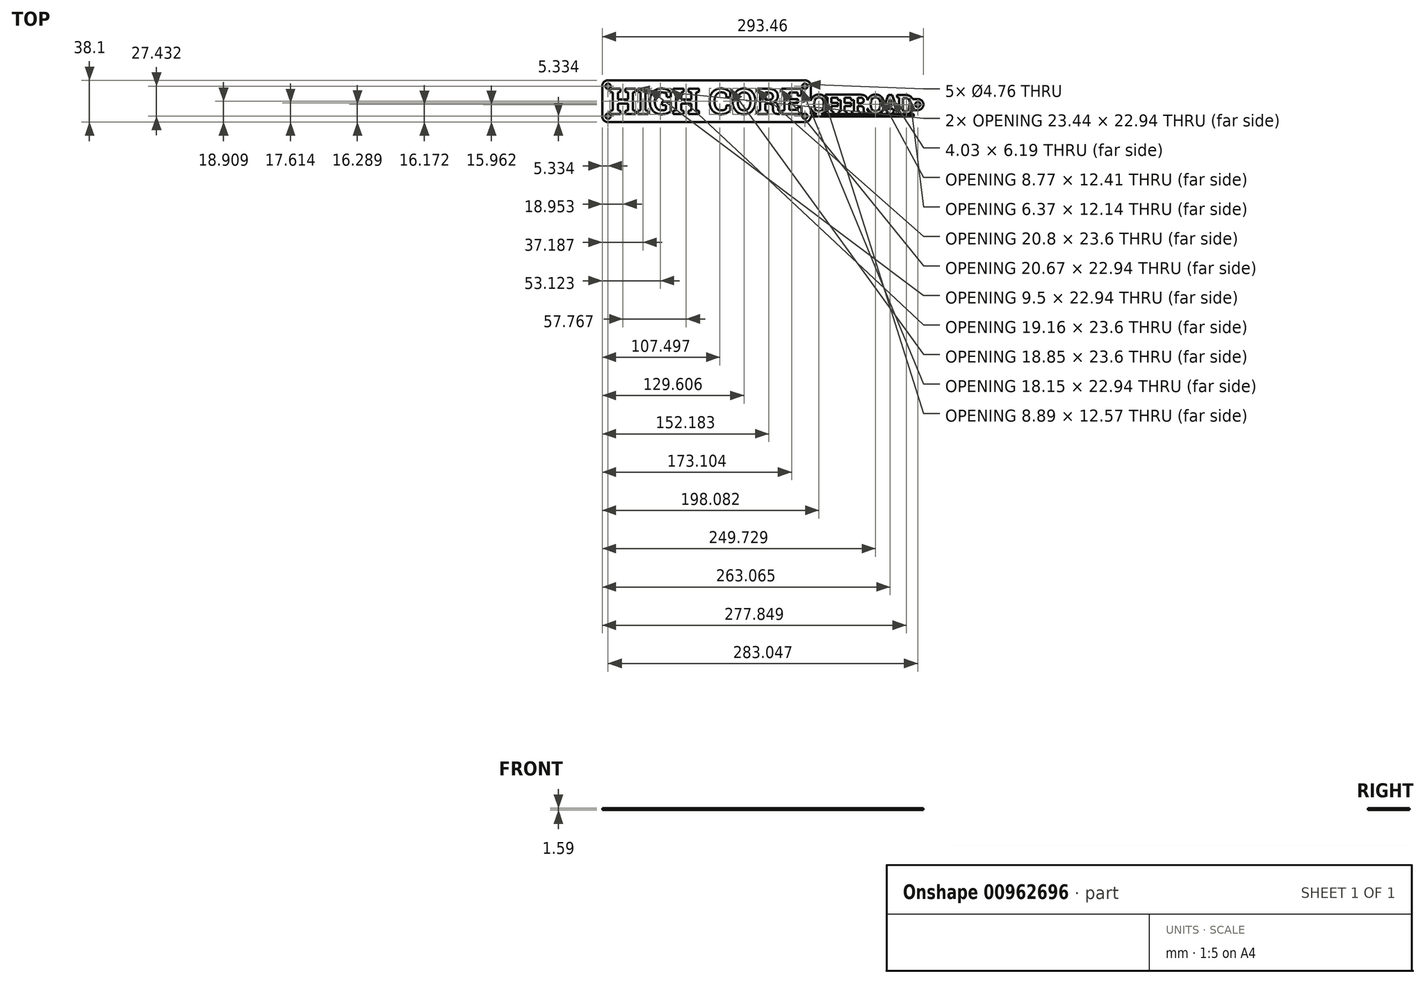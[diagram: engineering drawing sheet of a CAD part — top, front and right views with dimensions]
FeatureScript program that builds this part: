
annotation { "Feature Type Name" : "Feature", "Feature Type Description" : "" }
export const myFeature = defineFeature(function(context is Context, id is Id, definition is map)
    precondition{}
    {
        {
            var Q0;
            Q0=qCreatedBy(makeId("Top.planeOp"),FACE);
            var sketch = newSketch(context, id + "F0", { "sketchPlane" : qUnion([Q0])});
            skLineSegment(sketch, "E0.bottom", {"start": v(95.25, -19.05) * mm, "end": v(-95.25, -19.05) * mm});
            skLineSegment(sketch, "E0.top", {"start": v(95.25, 19.05) * mm, "end": v(-95.25, 19.05) * mm});
            skLineSegment(sketch, "E0.left", {"start": v(95.25, -19.05) * mm, "end": v(95.25, 19.05) * mm});
            skLineSegment(sketch, "E0.right", {"start": v(-95.25, -19.05) * mm, "end": v(-95.25, 19.05) * mm});
            skPoint(sketch, "E0.middle", {"position": v(0, 0) * mm});
            skSolve(sketch);
        }
        {
            var Q0;
            Q0=makeQuery(id+"F0.imprint","IMPRINT",FACE,{"disambiguationData":[TD([[makeQuery(id+"F0.imprint","IMPRINT",EDGE,{"derivedFrom":sQuery(id+"F0.wireOp",EDGE,"E0.bottom")}),-1.0]])]});
            extrude(context, id + "F1", {"entities" : qUnion([Q0]), "depth" : 1.59 * mm, "offsetDistance" : 25.4 * mm});
        }
        {
            var Q0;
            Q0=makeQuery(id+"F1.opExtrude","CAP_FACE",FACE,{"disambiguationData":[OSD([sQuery(id+"F0.wireOp",EDGE,"E0.bottom"),sQuery(id+"F0.wireOp",EDGE,"E0.top"),sQuery(id+"F0.wireOp",EDGE,"E0.left"),sQuery(id+"F0.wireOp",EDGE,"E0.right")])],"isStart":false});
            var sketch = newSketch(context, id + "F2", { "sketchPlane" : qUnion([Q0])});
            skText(sketch, "E1", { "text": "HIGH CORE", "fontName": "RobotoSlab-Bold.ttf"});
            skPoint(sketch, "E2", {"position": v(0, 0) * mm});
            skLineSegment(sketch, "E3", {"start": v(-89.92, 0) * mm, "end": v(0, 0) * mm, "construction": true});
            skLineSegment(sketch, "E4", {"start": v(0, 0) * mm, "end": v(89.92, 0) * mm, "construction": true});
            skLineSegment(sketch, "E5", {"start": v(-95.25, 19.05) * mm, "end": v(-88.39, 12.19) * mm, "construction": true});
            skLineSegment(sketch, "E6", {"start": v(-89.92, 0) * mm, "end": v(-89.92, 13.72) * mm, "construction": true});
            skCircle(sketch, "E7", {"center": v(-89.92, 13.72) * mm, "radius": 2.38 * mm});
            skCircle(sketch, "E8.MirrorC", {"center": v(-89.92, -13.72) * mm, "radius": 2.38 * mm});
            skCircle(sketch, "E9.MirrorC", {"center": v(89.92, 13.72) * mm, "radius": 2.38 * mm});
            skCircle(sketch, "E10.MirrorC", {"center": v(89.92, -13.72) * mm, "radius": 2.38 * mm});
            const initialGuessF2  = {"E1": [-0.0889, -0.01161, 1, 0, 0.02323]};
            skSetInitialGuess(sketch, initialGuessF2);
            skSolve(sketch);
        }
        {
            var Q0;
            Q0=qSketchRegion(id+"F2",true);
            extrude(context, id + "F3", {"entities" : qUnion([Q0]), "operationType" : NewBodyOperationType.REMOVE, "oppositeDirection" : true, "depth" : 25.4 * mm, "offsetDistance" : 25.4 * mm});
        }
        {
            var Q0;
            Q0=makeQuery(id+"F1.opExtrude","SWEPT_EDGE",EDGE,{"disambiguationData":[OSD([sQuery(id+"F0.wireOp",EDGE,"E0.top"),sQuery(id+"F0.wireOp",EDGE,"E0.right")])]});
            var Q1;
            Q1=makeQuery(id+"F1.opExtrude","SWEPT_EDGE",EDGE,{"disambiguationData":[OSD([sQuery(id+"F0.wireOp",EDGE,"E0.bottom"),sQuery(id+"F0.wireOp",EDGE,"E0.right")])]});
            var Q2;
            Q2=makeQuery(id+"F1.opExtrude","SWEPT_EDGE",EDGE,{"disambiguationData":[OSD([sQuery(id+"F0.wireOp",EDGE,"E0.top"),sQuery(id+"F0.wireOp",EDGE,"E0.left")])]});
            var Q3;
            Q3=makeQuery(id+"F1.opExtrude","SWEPT_EDGE",EDGE,{"disambiguationData":[OSD([sQuery(id+"F0.wireOp",EDGE,"E0.bottom"),sQuery(id+"F0.wireOp",EDGE,"E0.left")])]});
            fillet(context, id + "F4", {"entities" : qUnion([Q0, Q1, Q2, Q3]), "radius" : 5.08 * mm, "tangentPropagation" : true, "allowEdgeOverflow" : false});
        }
        {
            var Q0;
            Q0=makeQuery(id+"F1.opExtrude","CAP_FACE",FACE,{"disambiguationData":[OSD([sQuery(id+"F0.wireOp",EDGE,"E0.bottom"),sQuery(id+"F0.wireOp",EDGE,"E0.top"),sQuery(id+"F0.wireOp",EDGE,"E0.left"),sQuery(id+"F0.wireOp",EDGE,"E0.right")])],"isStart":false});
            var sketch = newSketch(context, id + "F5", { "sketchPlane" : qUnion([Q0])});
            skPoint(sketch, "E11", {"position": v(93.37, -3.45) * mm});
            skText(sketch, "E12", { "text": "O", "fontName": "RobotoSlab-Bold.ttf"});
            skText(sketch, "E13", { "text": "F", "fontName": "RobotoSlab-Bold.ttf"});
            skText(sketch, "E14", { "text": "F", "fontName": "RobotoSlab-Bold.ttf"});
            skText(sketch, "E15", { "text": "R", "fontName": "RobotoSlab-Bold.ttf"});
            skText(sketch, "E16", { "text": "O", "fontName": "RobotoSlab-Bold.ttf"});
            skText(sketch, "E17", { "text": "A", "fontName": "RobotoSlab-Bold.ttf"});
            skText(sketch, "E18", { "text": "D", "fontName": "RobotoSlab-Bold.ttf"});
            skLineSegment(sketch, "E19", {"start": v(87.12, -11.65) * mm, "end": v(189.23, -11.65) * mm});
            skLineSegment(sketch, "E20.0", {"start": v(95.25, -13.97) * mm, "end": v(95.25, 13.97) * mm});
            skLineSegment(sketch, "E21", {"start": v(95.25, -13.97) * mm, "end": v(189.23, -13.97) * mm});
            skLineSegment(sketch, "E22", {"start": v(189.23, -11.65) * mm, "end": v(189.23, -13.97) * mm});
            skLineSegment(sketch, "E23", {"start": v(95.25, -13.97) * mm, "end": v(95.25, -11.65) * mm});
            skLineSegment(sketch, "E24", {"start": v(95.25, -11.65) * mm, "end": v(189.23, -11.65) * mm});
            const initialGuessF5  = {"E12": [0.09406, -0.01165, 1, 0, 0.01778], "E13": [0.10804, -0.01165, 1, 0, 0.01778], "E14": [0.12013, -0.01165, 1, 0, 0.01778], "E15": [0.1322, -0.01165, 1, 0, 0.01778], "E16": [0.14582, -0.01142, 1, 0, 0.01755], "E17": [0.15894, -0.01186, 1, 0, 0.01778], "E18": [0.17335, -0.01186, 1, 0, 0.01778]};
            skSetInitialGuess(sketch, initialGuessF5);
            skSolve(sketch);
        }
        {
            var Q0;
            {var subQ2=sQuery(id+"F5.wireOp",EDGE,"E17.sketch_text.stroke-5");Q0=makeQuery(id+"F5.imprint","IMPRINT",FACE,{"disambiguationData":[TD([[makeQuery(id+"F5.imprint","IMPRINT",EDGE,{"derivedFrom":subQ2}),-1.0]])]});}
            var Q1;
            {var subQ6=sQuery(id+"F5.wireOp",EDGE,"E17.sketch_text.stroke-5");Q1=makeQuery(id+"F5.imprint","IMPRINT",FACE,{"disambiguationData":[TD([[makeQuery(id+"F5.imprint","IMPRINT",EDGE,{"derivedFrom":subQ6}),1.0]])]});}
            var Q2;
            {var subQ15=sQuery(id+"F5.wireOp",EDGE,"E17.sketch_text.stroke-2");Q2=makeQuery(id+"F5.imprint","IMPRINT",FACE,{"disambiguationData":[TD([[makeQuery(id+"F5.imprint","IMPRINT",EDGE,{"derivedFrom":subQ15}),-1.0]])]});}
            var Q3;
            {var subQ0=sQuery(id+"F5.wireOp",EDGE,"E16.sketch_text.stroke-1");var subQ1=sQuery(id+"F5.wireOp",EDGE,"E16.sketch_text.stroke-0");var subQ2=makeQuery(id+"F5.imprint","INTERSECT",VERTEX,{"derivedFrom":[subQ1,subQ0]});Q3=makeQuery(id+"F5.imprint","IMPRINT",FACE,{"disambiguationData":[TD([[makeQuery(id+"F5.imprint","IMPRINT",EDGE,{"disambiguationData":[TD([[subQ2,1.0]])],"derivedFrom":subQ1}),1.0]])]});}
            var Q4;
            {var subQ0=sQuery(id+"F5.wireOp",EDGE,"E17.sketch_text.stroke-15");var subQ1=sQuery(id+"F5.wireOp",EDGE,"E16.sketch_text.stroke-1");var subQ2=makeQuery(id+"F5.imprint","INTERSECT",VERTEX,{"derivedFrom":[subQ1,subQ0]});Q4=makeQuery(id+"F5.imprint","IMPRINT",FACE,{"disambiguationData":[TD([[makeQuery(id+"F5.imprint","IMPRINT",EDGE,{"disambiguationData":[TD([[subQ2,1.0]])],"derivedFrom":subQ1}),-1.0]])]});}
            var Q5;
            {var subQ9=sQuery(id+"F5.wireOp",EDGE,"E16.sketch_text.stroke-4");Q5=makeQuery(id+"F5.imprint","IMPRINT",FACE,{"disambiguationData":[TD([[makeQuery(id+"F5.imprint","IMPRINT",EDGE,{"derivedFrom":subQ9}),-1.0]])]});}
            var Q6;
            {var subQ0=sQuery(id+"F5.wireOp",EDGE,"E17.sketch_text.stroke-1");var subQ1=sQuery(id+"F5.wireOp",EDGE,"E16.sketch_text.stroke-0");var subQ2=makeQuery(id+"F5.imprint","INTERSECT",VERTEX,{"disambiguationData":[OD(0.0)],"derivedFrom":[subQ1,subQ0]});Q6=makeQuery(id+"F5.imprint","IMPRINT",FACE,{"disambiguationData":[TD([[makeQuery(id+"F5.imprint","IMPRINT",EDGE,{"disambiguationData":[TD([[subQ2,-1.0]])],"derivedFrom":subQ1}),-1.0]])]});}
            var Q7;
            {var subQ7=sQuery(id+"F5.wireOp",EDGE,"E14.sketch_text.stroke-5");Q7=makeQuery(id+"F5.imprint","IMPRINT",FACE,{"disambiguationData":[TD([[makeQuery(id+"F5.imprint","IMPRINT",EDGE,{"derivedFrom":subQ7}),1.0]])]});}
            var Q8;
            {var subQ0=sQuery(id+"F5.wireOp",EDGE,"E15.sketch_text.stroke-2");var subQ1=sQuery(id+"F5.wireOp",EDGE,"E15.sketch_text.stroke-1");var subQ2=makeQuery(id+"F5.imprint","INTERSECT",VERTEX,{"derivedFrom":[subQ1,subQ0]});Q8=makeQuery(id+"F5.imprint","IMPRINT",FACE,{"disambiguationData":[TD([[makeQuery(id+"F5.imprint","IMPRINT",EDGE,{"disambiguationData":[TD([[subQ2,1.0]])],"derivedFrom":subQ1}),-1.0]])]});}
            var Q9;
            {var subQ0=sQuery(id+"F5.wireOp",EDGE,"E16.sketch_text.stroke-3");var subQ1=sQuery(id+"F5.wireOp",EDGE,"E15.sketch_text.stroke-5");var subQ2=makeQuery(id+"F5.imprint","INTERSECT",VERTEX,{"disambiguationData":[OD(0.0)],"derivedFrom":[subQ1,subQ0]});Q9=makeQuery(id+"F5.imprint","IMPRINT",FACE,{"disambiguationData":[TD([[makeQuery(id+"F5.imprint","IMPRINT",EDGE,{"disambiguationData":[TD([[subQ2,-1.0]])],"derivedFrom":subQ1}),-1.0]])]});}
            var Q10;
            {var subQ2=sQuery(id+"F5.wireOp",EDGE,"E14.sketch_text.stroke-5");Q10=makeQuery(id+"F5.imprint","IMPRINT",FACE,{"disambiguationData":[TD([[makeQuery(id+"F5.imprint","IMPRINT",EDGE,{"derivedFrom":subQ2}),-1.0]])]});}
            var Q11;
            {var subQ1=sQuery(id+"F5.wireOp",EDGE,"E13.sketch_text.stroke-5");Q11=makeQuery(id+"F5.imprint","IMPRINT",FACE,{"disambiguationData":[TD([[makeQuery(id+"F5.imprint","IMPRINT",EDGE,{"derivedFrom":subQ1}),1.0]])]});}
            var Q12;
            {var subQ2=sQuery(id+"F5.wireOp",EDGE,"E13.sketch_text.stroke-5");Q12=makeQuery(id+"F5.imprint","IMPRINT",FACE,{"disambiguationData":[TD([[makeQuery(id+"F5.imprint","IMPRINT",EDGE,{"derivedFrom":subQ2}),-1.0]])]});}
            var Q13;
            {var subQ8=sQuery(id+"F5.wireOp",EDGE,"E12.sketch_text.stroke-9");Q13=makeQuery(id+"F5.imprint","IMPRINT",FACE,{"disambiguationData":[TD([[makeQuery(id+"F5.imprint","IMPRINT",EDGE,{"derivedFrom":subQ8}),1.0]])]});}
            var Q14;
            {var subQ0=sQuery(id+"F5.wireOp",EDGE,"E12.sketch_text.stroke-6");Q14=makeQuery(id+"F5.imprint","IMPRINT",FACE,{"disambiguationData":[TD([[makeQuery(id+"F5.imprint","IMPRINT",EDGE,{"derivedFrom":subQ0}),-1.0]])]});}
            var Q15;
            {var subQ5=sQuery(id+"F5.wireOp",EDGE,"E15.sketch_text.stroke-3");Q15=makeQuery(id+"F5.imprint","IMPRINT",FACE,{"disambiguationData":[TD([[makeQuery(id+"F5.imprint","IMPRINT",EDGE,{"derivedFrom":subQ5}),1.0]])]});}
            var Q16;
            Q16=makeQuery(id+"F5.imprint","IMPRINT",FACE,{"disambiguationData":[TD([[makeQuery(id+"F5.imprint","IMPRINT",EDGE,{"derivedFrom":sQuery(id+"F5.wireOp",EDGE,"E18.sketch_text.stroke-0")}),-1.0]])]});
            var Q17;
            {var subQ3=sQuery(id+"F5.wireOp",EDGE,"E17.sketch_text.stroke-4");var subQ5=sQuery(id+"F5.wireOp",EDGE,"E17.sketch_text.stroke-5");var subQ6=makeQuery(id+"F5.imprint","INTERSECT",VERTEX,{"derivedFrom":[subQ3,subQ5]});Q17=makeQuery(id+"F5.imprint","IMPRINT",FACE,{"disambiguationData":[TD([[makeQuery(id+"F5.imprint","IMPRINT",EDGE,{"disambiguationData":[TD([[subQ6,1.0]])],"derivedFrom":subQ3}),-1.0]])]});}
            extrude(context, id + "F6", {"entities" : qUnion([Q0, Q1, Q2, Q3, Q4, Q5, Q6, Q7, Q8, Q9, Q10, Q11, Q12, Q13, Q14, Q15, Q16, Q17]), "operationType" : NewBodyOperationType.ADD, "oppositeDirection" : true, "depth" : 1.59 * mm, "offsetDistance" : 25.4 * mm});
        }
        {
            var Q0;
            Q0=makeQuery(id+"F6.opExtrude","CAP_FACE",FACE,{"disambiguationData":[OSD([sQuery(id+"F5.wireOp",EDGE,"E12.sketch_text.stroke-0"),sQuery(id+"F5.wireOp",EDGE,"E12.sketch_text.stroke-8"),sQuery(id+"F5.wireOp",EDGE,"E12.sketch_text.stroke-9"),sQuery(id+"F5.wireOp",EDGE,"E13.sketch_text.stroke-0"),sQuery(id+"F5.wireOp",EDGE,"E13.sketch_text.stroke-1"),sQuery(id+"F5.wireOp",EDGE,"E13.sketch_text.stroke-2"),sQuery(id+"F5.wireOp",EDGE,"E13.sketch_text.stroke-3"),sQuery(id+"F5.wireOp",EDGE,"E13.sketch_text.stroke-4"),sQuery(id+"F5.wireOp",EDGE,"E13.sketch_text.stroke-6"),sQuery(id+"F5.wireOp",EDGE,"E13.sketch_text.stroke-7"),sQuery(id+"F5.wireOp",EDGE,"E13.sketch_text.stroke-8"),sQuery(id+"F5.wireOp",EDGE,"E13.sketch_text.stroke-9"),sQuery(id+"F5.wireOp",EDGE,"E13.sketch_text.stroke-10"),sQuery(id+"F5.wireOp",EDGE,"E13.sketch_text.stroke-11"),sQuery(id+"F5.wireOp",EDGE,"E13.sketch_text.stroke-12"),sQuery(id+"F5.wireOp",EDGE,"E13.sketch_text.stroke-13"),sQuery(id+"F5.wireOp",EDGE,"E13.sketch_text.stroke-14"),sQuery(id+"F5.wireOp",EDGE,"E13.sketch_text.stroke-15"),sQuery(id+"F5.wireOp",EDGE,"E13.sketch_text.stroke-17"),sQuery(id+"F5.wireOp",EDGE,"E14.sketch_text.stroke-0"),sQuery(id+"F5.wireOp",EDGE,"E14.sketch_text.stroke-1"),sQuery(id+"F5.wireOp",EDGE,"E14.sketch_text.stroke-4"),sQuery(id+"F5.wireOp",EDGE,"E14.sketch_text.stroke-6"),sQuery(id+"F5.wireOp",EDGE,"E14.sketch_text.stroke-7"),sQuery(id+"F5.wireOp",EDGE,"E14.sketch_text.stroke-8"),sQuery(id+"F5.wireOp",EDGE,"E14.sketch_text.stroke-9"),sQuery(id+"F5.wireOp",EDGE,"E14.sketch_text.stroke-10"),sQuery(id+"F5.wireOp",EDGE,"E14.sketch_text.stroke-11"),sQuery(id+"F5.wireOp",EDGE,"E14.sketch_text.stroke-12"),sQuery(id+"F5.wireOp",EDGE,"E14.sketch_text.stroke-13"),sQuery(id+"F5.wireOp",EDGE,"E14.sketch_text.stroke-14"),sQuery(id+"F5.wireOp",EDGE,"E14.sketch_text.stroke-15"),sQuery(id+"F5.wireOp",EDGE,"E14.sketch_text.stroke-17"),sQuery(id+"F5.wireOp",EDGE,"E15.sketch_text.stroke-0"),sQuery(id+"F5.wireOp",EDGE,"E15.sketch_text.stroke-1"),sQuery(id+"F5.wireOp",EDGE,"E15.sketch_text.stroke-5"),sQuery(id+"F5.wireOp",EDGE,"E15.sketch_text.stroke-6"),sQuery(id+"F5.wireOp",EDGE,"E15.sketch_text.stroke-7"),sQuery(id+"F5.wireOp",EDGE,"E15.sketch_text.stroke-8"),sQuery(id+"F5.wireOp",EDGE,"E15.sketch_text.stroke-9"),sQuery(id+"F5.wireOp",EDGE,"E15.sketch_text.stroke-10"),sQuery(id+"F5.wireOp",EDGE,"E15.sketch_text.stroke-12"),sQuery(id+"F5.wireOp",EDGE,"E15.sketch_text.stroke-13"),sQuery(id+"F5.wireOp",EDGE,"E15.sketch_text.stroke-14"),sQuery(id+"F5.wireOp",EDGE,"E15.sketch_text.stroke-15"),sQuery(id+"F5.wireOp",EDGE,"E15.sketch_text.stroke-16"),sQuery(id+"F5.wireOp",EDGE,"E15.sketch_text.stroke-17"),sQuery(id+"F5.wireOp",EDGE,"E15.sketch_text.stroke-18"),sQuery(id+"F5.wireOp",EDGE,"E15.sketch_text.stroke-19"),sQuery(id+"F5.wireOp",EDGE,"E15.sketch_text.stroke-20"),sQuery(id+"F5.wireOp",EDGE,"E15.sketch_text.stroke-22"),sQuery(id+"F5.wireOp",EDGE,"E15.sketch_text.stroke-23"),sQuery(id+"F5.wireOp",EDGE,"E15.sketch_text.stroke-24"),sQuery(id+"F5.wireOp",EDGE,"E15.sketch_text.stroke-27"),sQuery(id+"F5.wireOp",EDGE,"E15.sketch_text.stroke-28"),sQuery(id+"F5.wireOp",EDGE,"E15.sketch_text.stroke-29"),sQuery(id+"F5.wireOp",EDGE,"E15.sketch_text.stroke-30"),sQuery(id+"F5.wireOp",EDGE,"E15.sketch_text.stroke-31"),sQuery(id+"F5.wireOp",EDGE,"E15.sketch_text.stroke-32"),sQuery(id+"F5.wireOp",EDGE,"E15.sketch_text.stroke-33"),sQuery(id+"F5.wireOp",EDGE,"E15.sketch_text.stroke-34"),sQuery(id+"F5.wireOp",EDGE,"E15.sketch_text.stroke-35"),sQuery(id+"F5.wireOp",EDGE,"E16.sketch_text.stroke-0"),sQuery(id+"F5.wireOp",EDGE,"E16.sketch_text.stroke-1"),sQuery(id+"F5.wireOp",EDGE,"E16.sketch_text.stroke-2"),sQuery(id+"F5.wireOp",EDGE,"E16.sketch_text.stroke-3"),sQuery(id+"F5.wireOp",EDGE,"E16.sketch_text.stroke-5"),sQuery(id+"F5.wireOp",EDGE,"E16.sketch_text.stroke-6"),sQuery(id+"F5.wireOp",EDGE,"E16.sketch_text.stroke-7"),sQuery(id+"F5.wireOp",EDGE,"E16.sketch_text.stroke-8"),sQuery(id+"F5.wireOp",EDGE,"E16.sketch_text.stroke-9"),sQuery(id+"F5.wireOp",EDGE,"E16.sketch_text.stroke-10"),sQuery(id+"F5.wireOp",EDGE,"E16.sketch_text.stroke-11"),sQuery(id+"F5.wireOp",EDGE,"E16.sketch_text.stroke-12"),sQuery(id+"F5.wireOp",EDGE,"E16.sketch_text.stroke-13"),sQuery(id+"F5.wireOp",EDGE,"E16.sketch_text.stroke-14"),sQuery(id+"F5.wireOp",EDGE,"E16.sketch_text.stroke-15"),sQuery(id+"F5.wireOp",EDGE,"E16.sketch_text.stroke-16"),sQuery(id+"F5.wireOp",EDGE,"E16.sketch_text.stroke-17"),sQuery(id+"F5.wireOp",EDGE,"E16.sketch_text.stroke-18"),sQuery(id+"F5.wireOp",EDGE,"E16.sketch_text.stroke-19"),sQuery(id+"F5.wireOp",EDGE,"E17.sketch_text.stroke-1"),sQuery(id+"F5.wireOp",EDGE,"E17.sketch_text.stroke-2"),sQuery(id+"F5.wireOp",EDGE,"E17.sketch_text.stroke-3"),sQuery(id+"F5.wireOp",EDGE,"E17.sketch_text.stroke-4"),sQuery(id+"F5.wireOp",EDGE,"E17.sketch_text.stroke-6"),sQuery(id+"F5.wireOp",EDGE,"E17.sketch_text.stroke-7"),sQuery(id+"F5.wireOp",EDGE,"E17.sketch_text.stroke-8"),sQuery(id+"F5.wireOp",EDGE,"E17.sketch_text.stroke-9"),sQuery(id+"F5.wireOp",EDGE,"E17.sketch_text.stroke-10"),sQuery(id+"F5.wireOp",EDGE,"E17.sketch_text.stroke-11"),sQuery(id+"F5.wireOp",EDGE,"E17.sketch_text.stroke-12"),sQuery(id+"F5.wireOp",EDGE,"E17.sketch_text.stroke-13"),sQuery(id+"F5.wireOp",EDGE,"E17.sketch_text.stroke-14"),sQuery(id+"F5.wireOp",EDGE,"E17.sketch_text.stroke-15"),sQuery(id+"F5.wireOp",EDGE,"E17.sketch_text.stroke-16"),sQuery(id+"F5.wireOp",EDGE,"E17.sketch_text.stroke-17"),sQuery(id+"F5.wireOp",EDGE,"E17.sketch_text.stroke-18"),sQuery(id+"F5.wireOp",EDGE,"E17.sketch_text.stroke-19"),sQuery(id+"F5.wireOp",EDGE,"E18.sketch_text.stroke-0"),sQuery(id+"F5.wireOp",EDGE,"E18.sketch_text.stroke-1"),sQuery(id+"F5.wireOp",EDGE,"E18.sketch_text.stroke-2"),sQuery(id+"F5.wireOp",EDGE,"E18.sketch_text.stroke-3"),sQuery(id+"F5.wireOp",EDGE,"E18.sketch_text.stroke-4"),sQuery(id+"F5.wireOp",EDGE,"E18.sketch_text.stroke-5"),sQuery(id+"F5.wireOp",EDGE,"E18.sketch_text.stroke-7"),sQuery(id+"F5.wireOp",EDGE,"E18.sketch_text.stroke-8"),sQuery(id+"F5.wireOp",EDGE,"E18.sketch_text.stroke-9"),sQuery(id+"F5.wireOp",EDGE,"E18.sketch_text.stroke-10"),sQuery(id+"F5.wireOp",EDGE,"E18.sketch_text.stroke-11"),sQuery(id+"F5.wireOp",EDGE,"E18.sketch_text.stroke-12"),sQuery(id+"F5.wireOp",EDGE,"E18.sketch_text.stroke-13"),sQuery(id+"F5.wireOp",EDGE,"E18.sketch_text.stroke-14"),sQuery(id+"F5.wireOp",EDGE,"E18.sketch_text.stroke-15"),sQuery(id+"F5.wireOp",EDGE,"E18.sketch_text.stroke-16"),sQuery(id+"F5.wireOp",EDGE,"E18.sketch_text.stroke-17"),sQuery(id+"F5.wireOp",EDGE,"E18.sketch_text.stroke-18"),sQuery(id+"F5.wireOp",EDGE,"E18.sketch_text.stroke-19"),sQuery(id+"F5.wireOp",EDGE,"E18.sketch_text.stroke-20"),sQuery(id+"F5.wireOp",EDGE,"E24")])],"isStart":true});
            var sketch = newSketch(context, id + "F7", { "sketchPlane" : qUnion([Q0])});
            skLineSegment(sketch, "E25", {"start": v(189.32, -3.09) * mm, "end": v(193.13, -3.09) * mm, "construction": true});
            skCircle(sketch, "E26", {"center": v(193.13, -3.09) * mm, "radius": 2.38 * mm});
            skCircle(sketch, "E27", {"center": v(193.13, -3.09) * mm, "radius": 5.08 * mm});
            skLineSegment(sketch, "E28", {"start": v(193.13, 2) * mm, "end": v(187.45, 2) * mm});
            skLineSegment(sketch, "E29", {"start": v(193.13, -8.17) * mm, "end": v(187.5, -8.17) * mm});
            skLineSegment(sketch, "E30", {"start": v(187.5, -8.17) * mm, "end": v(187.45, 2) * mm});
            skSolve(sketch);
        }
        {
            var Q0;
            Q0=makeQuery(id+"F5.imprint","IMPRINT",FACE,{"disambiguationData":[TD([[makeQuery(id+"F5.imprint","IMPRINT",EDGE,{"derivedFrom":sQuery(id+"F5.wireOp",EDGE,"E21")}),1.0]])]});
            var Q1;
            {var subQ0=sQuery(id+"F5.wireOp",EDGE,"E12.sketch_text.stroke-2");var subQ1=sQuery(id+"F5.wireOp",EDGE,"E12.sketch_text.stroke-1");var subQ2=makeQuery(id+"F5.imprint","INTERSECT",VERTEX,{"derivedFrom":[subQ1,subQ0]});Q1=makeQuery(id+"F5.imprint","IMPRINT",FACE,{"disambiguationData":[TD([[makeQuery(id+"F5.imprint","IMPRINT",EDGE,{"disambiguationData":[TD([[subQ2,1.0]])],"derivedFrom":subQ1}),-1.0]])]});}
            var Q2;
            {var subQ0=sQuery(id+"F7.wireOp",EDGE,"E28");var subQ1=sQuery(id+"F7.wireOp",EDGE,"E27");var subQ2=makeQuery(id+"F7.imprint","INTERSECT",VERTEX,{"derivedFrom":[subQ1,subQ0]});Q2=makeQuery(id+"F7.imprint","IMPRINT",FACE,{"disambiguationData":[TD([[makeQuery(id+"F7.imprint","IMPRINT",EDGE,{"disambiguationData":[TD([[subQ2,-1.0]])],"derivedFrom":subQ1}),-1.0]])]});}
            var Q3;
            Q3=makeQuery(id+"F7.imprint","IMPRINT",FACE,{"disambiguationData":[TD([[makeQuery(id+"F7.imprint","IMPRINT",EDGE,{"derivedFrom":sQuery(id+"F7.wireOp",EDGE,"E26")}),-1.0]])]});
            var Q4;
            {var subQ0=sQuery(id+"F7.wireOp",EDGE,"E29");var subQ1=sQuery(id+"F7.wireOp",EDGE,"E27");var subQ2=makeQuery(id+"F7.imprint","INTERSECT",VERTEX,{"derivedFrom":[subQ1,subQ0]});Q4=makeQuery(id+"F7.imprint","IMPRINT",FACE,{"disambiguationData":[TD([[makeQuery(id+"F7.imprint","IMPRINT",EDGE,{"disambiguationData":[TD([[subQ2,1.0]])],"derivedFrom":subQ1}),-1.0]])]});}
            extrude(context, id + "F8", {"entities" : qUnion([Q0, Q1, Q2, Q3, Q4]), "operationType" : NewBodyOperationType.ADD, "oppositeDirection" : true, "depth" : 1.59 * mm, "offsetDistance" : 25.4 * mm});
        }
    });
